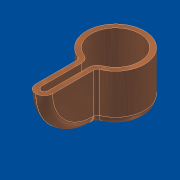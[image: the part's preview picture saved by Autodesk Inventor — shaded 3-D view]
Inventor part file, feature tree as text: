
AUTODESK INVENTOR PART (.ipt)
format: ipt  version: unknown  size: 331,264 bytes
history: native  units: mm
features: sketch x5, extrude x3, other x2, projected_geometry x2, plane x1, fillet x1, revolve x1, delete_face x1, thicken_offset x1, hole x1
ambient origin geometry x8: Origin, YZ Plane, XZ Plane, XY Plane, X Axis, Y Axis, Z Axis, Center Point
feature tree (18):
  extrude  "Extrusion1"  Depth=10.0mm TaperAngle=0.0deg
  plane  "Work Plane1"
  extrude  "Extrusion2"  Depth=10.0mm TaperAngle=0.0deg
  extrude  "Extrusion3"  Depth=3.6mm
  fillet  "Fillet1"  Radius=1.5mm
  revolve  "Revolution1"  [1 undecoded]
  delete_face  "Delete Face1"
  thicken_offset  "Thicken1"
  hole  "Hole1"  [1 undecoded]
  sketch  "Sketch1"  dims[d0=10.0mm d1=0.0mm d2=10.0mm d3=0.0mm]
  other  "Work Axis1"
  other  "Work Axis2"
  sketch  "Sketch2"  dims[d4=20.0mm d5=10.0mm d6=0.0mm]
  sketch  "Sketch3"  dims[d7=1.74mm d8=3.6mm d9=1.5mm]
  projected_geometry  "Projected Loop1"
  projected_geometry  "Projected Loop2"
  sketch  "Sketch4"  dims[d10=90.0deg d11=1.0mm]
  sketch  "Sketch5"  dims[d12=2.0mm d13=6.0mm d14=4.0mm d15=2.0mm d16=90.0deg d17=8.0mm d18=20.594885mm]
note: 2 required parameter values undecoded (feature->parameter linkage not recoverable at this tier; creation-order binding heuristic only, values carry confidence <= 0.55)